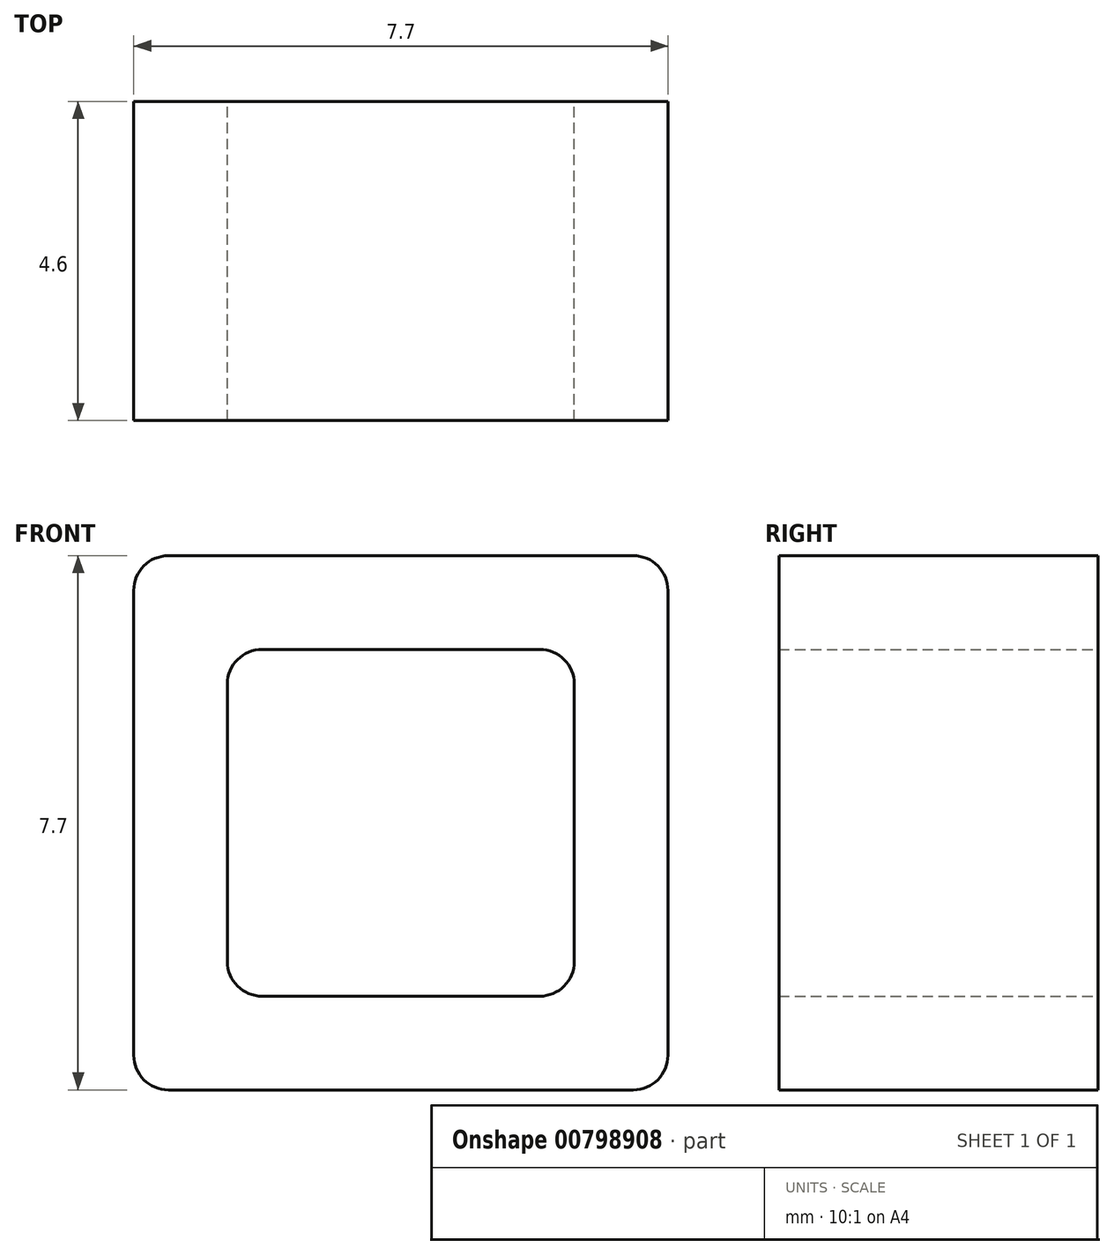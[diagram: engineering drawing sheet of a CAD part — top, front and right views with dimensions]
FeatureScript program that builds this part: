
annotation { "Feature Type Name" : "Feature", "Feature Type Description" : "" }
export const myFeature = defineFeature(function(context is Context, id is Id, definition is map)
    precondition{}
    {
        {
            var Q0;
            Q0=qCreatedBy(makeId("Front.planeOp"),FACE);
            var sketch = newSketch(context, id + "F0", { "sketchPlane" : qUnion([Q0])});
            skLineSegment(sketch, "E0.bottom", {"start": v(3.85, -3.85) * mm, "end": v(-3.85, -3.85) * mm});
            skLineSegment(sketch, "E0.top", {"start": v(3.85, 3.85) * mm, "end": v(-3.85, 3.85) * mm});
            skLineSegment(sketch, "E0.left", {"start": v(3.85, -3.85) * mm, "end": v(3.85, 3.85) * mm});
            skLineSegment(sketch, "E0.right", {"start": v(-3.85, -3.85) * mm, "end": v(-3.85, 3.85) * mm});
            skPoint(sketch, "E0.middle", {"position": v(0, 0) * mm});
            skLineSegment(sketch, "E1.bottom", {"start": v(2.5, -2.5) * mm, "end": v(-2.5, -2.5) * mm});
            skLineSegment(sketch, "E1.top", {"start": v(2.5, 2.5) * mm, "end": v(-2.5, 2.5) * mm});
            skLineSegment(sketch, "E1.left", {"start": v(2.5, -2.5) * mm, "end": v(2.5, 2.5) * mm});
            skLineSegment(sketch, "E1.right", {"start": v(-2.5, -2.5) * mm, "end": v(-2.5, 2.5) * mm});
            skSolve(sketch);
        }
        {
            var Q0;
            Q0=makeQuery(id+"F0.imprint","IMPRINT",FACE,{"disambiguationData":[TD([[makeQuery(id+"F0.imprint","IMPRINT",EDGE,{"derivedFrom":sQuery(id+"F0.wireOp",EDGE,"E0.bottom")}),-1.0]])]});
            extrude(context, id + "F1", {"entities" : qUnion([Q0]), "depth" : 4.6 * mm, "offsetDistance" : 25 * mm});
        }
        {
            var Q0;
            Q0=makeQuery(id+"F1.opExtrude","SWEPT_EDGE",EDGE,{"disambiguationData":[OSD([sQuery(id+"F0.wireOp",EDGE,"E1.top"),sQuery(id+"F0.wireOp",EDGE,"E1.left")])]});
            var Q1;
            Q1=makeQuery(id+"F1.opExtrude","SWEPT_EDGE",EDGE,{"disambiguationData":[OSD([sQuery(id+"F0.wireOp",EDGE,"E1.top"),sQuery(id+"F0.wireOp",EDGE,"E1.right")])]});
            var Q2;
            Q2=makeQuery(id+"F1.opExtrude","SWEPT_EDGE",EDGE,{"disambiguationData":[OSD([sQuery(id+"F0.wireOp",EDGE,"E1.bottom"),sQuery(id+"F0.wireOp",EDGE,"E1.left")])]});
            var Q3;
            Q3=makeQuery(id+"F1.opExtrude","SWEPT_EDGE",EDGE,{"disambiguationData":[OSD([sQuery(id+"F0.wireOp",EDGE,"E1.bottom"),sQuery(id+"F0.wireOp",EDGE,"E1.right")])]});
            fillet(context, id + "F2", {"entities" : qUnion([Q0, Q1, Q2, Q3]), "radius" : .5 * mm, "tangentPropagation" : true, "allowEdgeOverflow" : false});
        }
        {
            var Q0;
            Q0=makeQuery(id+"F1.opExtrude","SWEPT_EDGE",EDGE,{"disambiguationData":[OSD([sQuery(id+"F0.wireOp",EDGE,"E0.top"),sQuery(id+"F0.wireOp",EDGE,"E0.left")])]});
            var Q1;
            Q1=makeQuery(id+"F1.opExtrude","SWEPT_EDGE",EDGE,{"disambiguationData":[OSD([sQuery(id+"F0.wireOp",EDGE,"E0.bottom"),sQuery(id+"F0.wireOp",EDGE,"E0.left")])]});
            var Q2;
            Q2=makeQuery(id+"F1.opExtrude","SWEPT_EDGE",EDGE,{"disambiguationData":[OSD([sQuery(id+"F0.wireOp",EDGE,"E0.bottom"),sQuery(id+"F0.wireOp",EDGE,"E0.right")])]});
            var Q3;
            Q3=makeQuery(id+"F1.opExtrude","SWEPT_EDGE",EDGE,{"disambiguationData":[OSD([sQuery(id+"F0.wireOp",EDGE,"E0.top"),sQuery(id+"F0.wireOp",EDGE,"E0.right")])]});
            fillet(context, id + "F3", {"entities" : qUnion([Q0, Q1, Q2, Q3]), "radius" : .5 * mm, "tangentPropagation" : true, "allowEdgeOverflow" : false});
        }
    });
